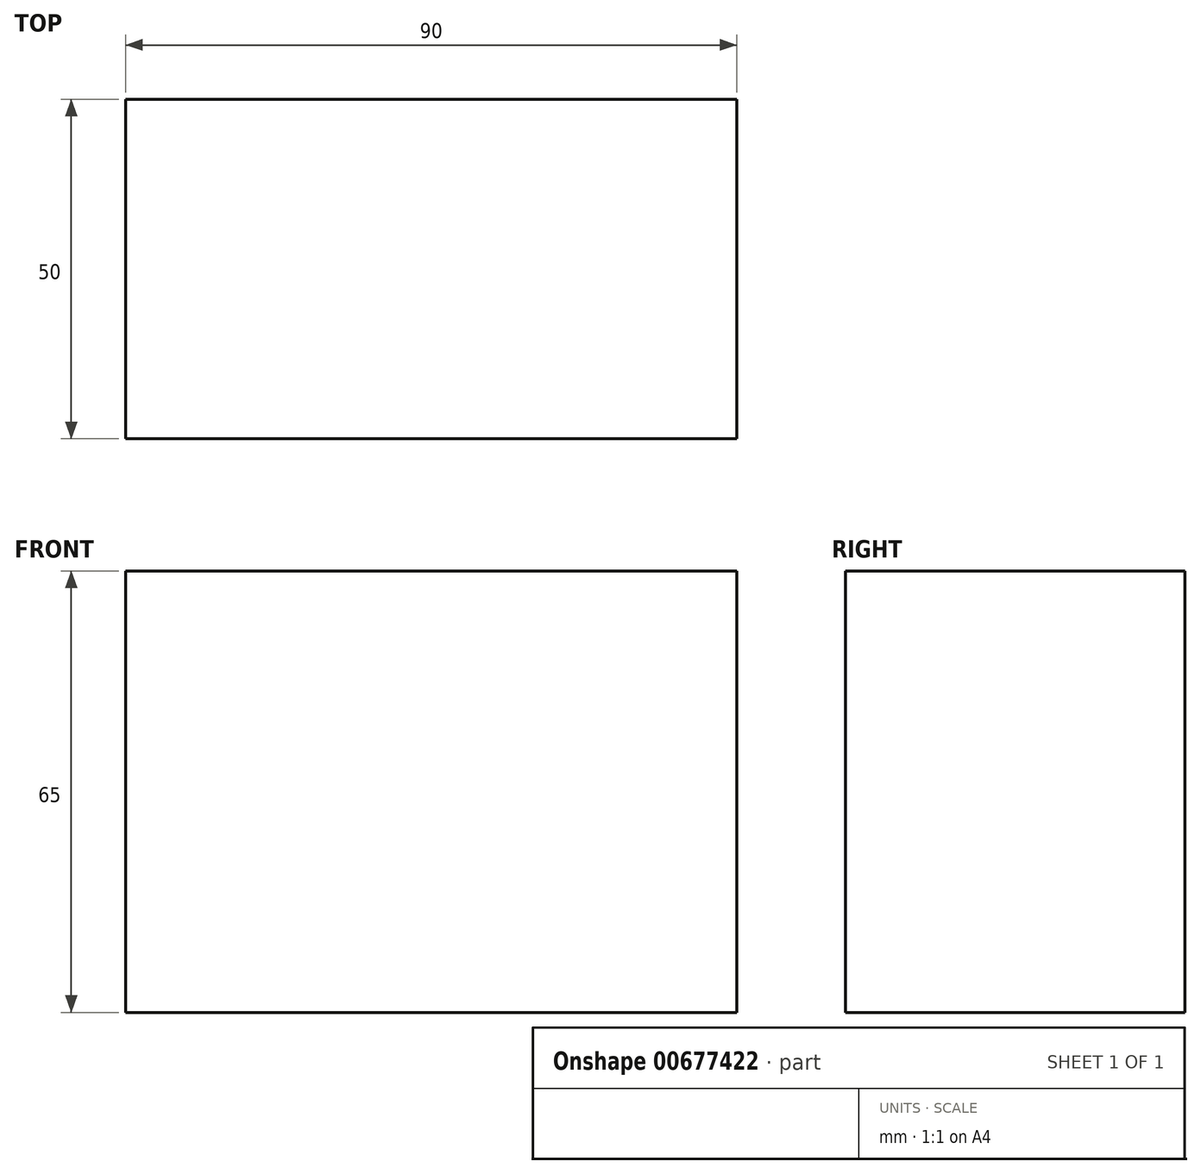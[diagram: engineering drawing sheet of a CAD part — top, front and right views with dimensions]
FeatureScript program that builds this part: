
annotation { "Feature Type Name" : "Feature", "Feature Type Description" : "" }
export const myFeature = defineFeature(function(context is Context, id is Id, definition is map)
    precondition{}
    {
        {
            var Q0;
            Q0=qCreatedBy(makeId("Front.planeOp"),FACE);
            var sketch = newSketch(context, id + "F0", { "sketchPlane" : qUnion([Q0])});
            skLineSegment(sketch, "E0.bottom", {"start": v(45, 32.5) * mm, "end": v(-45, 32.5) * mm});
            skLineSegment(sketch, "E0.top", {"start": v(45, -32.5) * mm, "end": v(-45, -32.5) * mm});
            skLineSegment(sketch, "E0.left", {"start": v(45, 32.5) * mm, "end": v(45, -32.5) * mm});
            skLineSegment(sketch, "E0.right", {"start": v(-45, 32.5) * mm, "end": v(-45, -32.5) * mm});
            skPoint(sketch, "E0.middle", {"position": v(0, 0) * mm});
            skSolve(sketch);
        }
        {
            var Q0;
            Q0=makeQuery(id+"F0.imprint","IMPRINT",FACE,{"disambiguationData":[TD([[makeQuery(id+"F0.imprint","IMPRINT",EDGE,{"derivedFrom":sQuery(id+"F0.wireOp",EDGE,"E0.bottom")}),1.0]])]});
            extrude(context, id + "F1", {"entities" : qUnion([Q0]), "depth" : 50 * mm, "offsetDistance" : 25 * mm});
        }
    });
